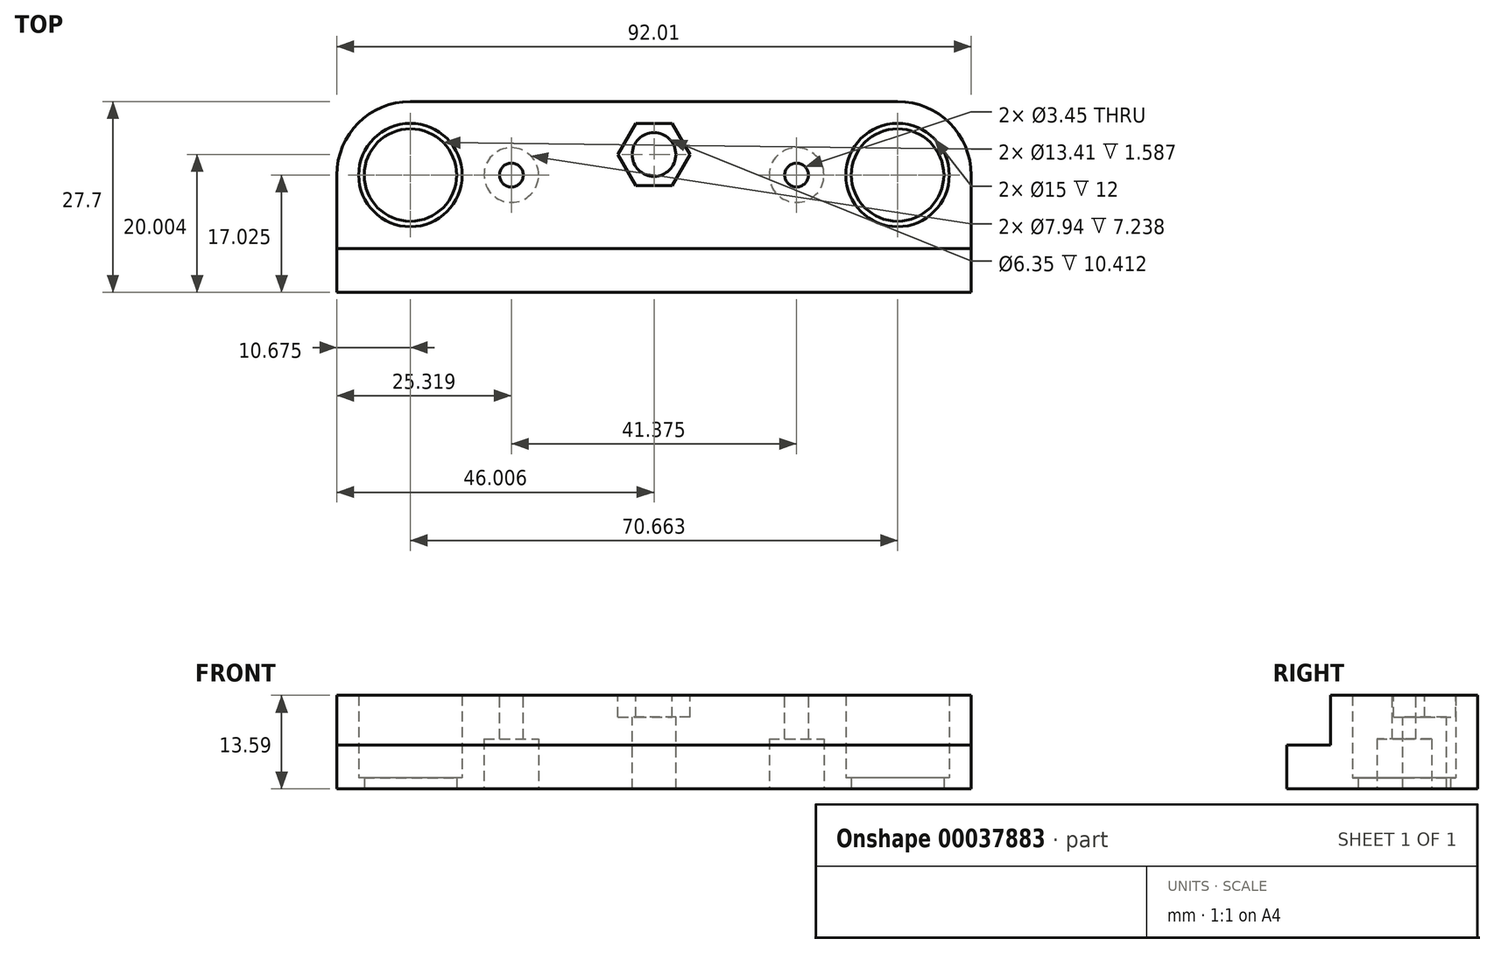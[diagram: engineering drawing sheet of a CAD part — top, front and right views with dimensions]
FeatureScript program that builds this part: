
annotation { "Feature Type Name" : "Feature", "Feature Type Description" : "" }
export const myFeature = defineFeature(function(context is Context, id is Id, definition is map)
    precondition{}
    {
        {
            var Q0;
            Q0=qCreatedBy(makeId("Top.planeOp"),FACE);
            var sketch = newSketch(context, id + "F0", { "sketchPlane" : qUnion([Q0])});
            skLineSegment(sketch, "E0.bottom", {"start": v(0, 0) * mm, "end": v(92.01, 0) * mm});
            skLineSegment(sketch, "E0.top", {"start": v(0, -27.7) * mm, "end": v(92.01, -27.7) * mm});
            skLineSegment(sketch, "E0.left", {"start": v(0, 0) * mm, "end": v(0, -27.7) * mm});
            skLineSegment(sketch, "E0.right", {"start": v(92.01, 0) * mm, "end": v(92.01, -27.7) * mm});
            skLineSegment(sketch, "E1", {"start": v(10.67, 0) * mm, "end": v(10.67, -10.67) * mm, "construction": true});
            skLineSegment(sketch, "E2", {"start": v(10.67, -10.67) * mm, "end": v(0, -10.67) * mm, "construction": true});
            skLineSegment(sketch, "E3", {"start": v(92.01, -10.67) * mm, "end": v(81.34, -10.67) * mm, "construction": true});
            skCircle(sketch, "E4", {"center": v(10.67, -10.67) * mm, "radius": 6.7 * mm});
            skCircle(sketch, "E5", {"center": v(81.34, -10.67) * mm, "radius": 6.7 * mm});
            skSolve(sketch);
        }
        {
            var Q0;
            Q0 = qSketchRegion(id + "F0", true);
            extrude(context, id + "F1", {"entities" : qUnion([Q0]), "depth" : 1.59 * mm});
        }
        {
            var Q0;
            Q0=makeQuery(id+"F1.opExtrude","SWEPT_EDGE",EDGE,{"disambiguationData":[OSD([sQuery(id+"F0.wireOp",EDGE,"E0.bottom"),sQuery(id+"F0.wireOp",EDGE,"E0.left")])]});
            var Q1;
            Q1=makeQuery(id+"F1.opExtrude","SWEPT_EDGE",EDGE,{"disambiguationData":[OSD([sQuery(id+"F0.wireOp",EDGE,"E0.bottom"),sQuery(id+"F0.wireOp",EDGE,"E0.right")])]});
            fillet(context, id + "F2", {"entities" : qUnion([Q0, Q1]), "radius" : 10.67 * mm, "tangentPropagation" : true, "allowEdgeOverflow" : false});
        }
        {
            var Q0;
            Q0=makeQuery(id+"F1.opExtrude","CAP_FACE",FACE,{"disambiguationData":[OSD([sQuery(id+"F0.wireOp",EDGE,"E0.bottom"),sQuery(id+"F0.wireOp",EDGE,"E0.top"),sQuery(id+"F0.wireOp",EDGE,"E0.left"),sQuery(id+"F0.wireOp",EDGE,"E0.right"),sQuery(id+"F0.wireOp",EDGE,"E4"),sQuery(id+"F0.wireOp",EDGE,"E5")])],"isStart":false});
            var sketch = newSketch(context, id + "F3", { "sketchPlane" : qUnion([Q0])});
            skLineSegment(sketch, "E6.bottom", {"start": v(0, -10.67) * mm, "end": v(92.01, -10.67) * mm, "construction": true});
            skLineSegment(sketch, "E6.top", {"start": v(0, -21.35) * mm, "end": v(92.01, -21.35) * mm});
            skLineSegment(sketch, "E6.left", {"start": v(0, -10.67) * mm, "end": v(0, -21.35) * mm});
            skLineSegment(sketch, "E6.right", {"start": v(92.01, -10.67) * mm, "end": v(92.01, -21.35) * mm});
            skLineSegment(sketch, "E7", {"start": v(46, -21.35) * mm, "end": v(46, -27.7) * mm, "construction": true});
            skPoint(sketch, "E7.endSnap0", {"position": v(46, -27.7) * mm});
            skCircle(sketch, "E8", {"center": v(10.67, -10.67) * mm, "radius": 7.5 * mm});
            skCircle(sketch, "E9", {"center": v(81.34, -10.67) * mm, "radius": 7.5 * mm});
            skSolve(sketch);
        }
        {
            var Q0;
            Q0=makeQuery(id+"F3.imprint","IMPRINT",FACE,{"disambiguationData":[TD([[makeQuery(id+"F3.imprint","IMPRINT",EDGE,{"derivedFrom":sQuery(id+"F3.wireOp",EDGE,"E6.top")}),1.0]])]});
            extrude(context, id + "F4", {"entities" : qUnion([Q0]), "operationType" : NewBodyOperationType.ADD, "depth" : 12 * mm});
        }
        {
            var Q0;
            {var subQ0=sQuery(id+"F0.wireOp",EDGE,"E0.top");var subQ1=sQuery(id+"F0.wireOp",EDGE,"E0.left");var subQ2=sQuery(id+"F0.wireOp",EDGE,"E0.right");Q0=makeQuery(id+"F4.boolean.opBoolean","SPLIT",FACE,{"disambiguationData":[TD([makeQuery(id+"F1.opExtrude","SWEPT_FACE",FACE,{"disambiguationData":[OSD([subQ0])]})])],"derivedFrom":makeQuery(id+"F1.opExtrude","CAP_FACE",FACE,{"disambiguationData":[OSD([sQuery(id+"F0.wireOp",EDGE,"E0.bottom"),subQ0,subQ1,subQ2,sQuery(id+"F0.wireOp",EDGE,"E4"),sQuery(id+"F0.wireOp",EDGE,"E5")])],"isStart":false})});}
            extrude(context, id + "F5", {"entities" : qUnion([Q0]), "operationType" : NewBodyOperationType.ADD, "depth" : 4.76 * mm});
        }
        {
            var Q0;
            Q0=makeQuery(id+"F4.opExtrude","CAP_FACE",FACE,{"disambiguationData":[OSD([sQuery(id+"F0.wireOp",EDGE,"E0.bottom"),sQuery(id+"F0.wireOp",EDGE,"E0.top"),sQuery(id+"F0.wireOp",EDGE,"E0.left"),sQuery(id+"F0.wireOp",EDGE,"E0.right"),sQuery(id+"F0.wireOp",EDGE,"E4"),sQuery(id+"F0.wireOp",EDGE,"E5"),sQuery(id+"F3.wireOp",EDGE,"E6.top"),sQuery(id+"F3.wireOp",EDGE,"E6.left"),sQuery(id+"F3.wireOp",EDGE,"E6.right"),sQuery(id+"F3.wireOp",EDGE,"E8"),sQuery(id+"F3.wireOp",EDGE,"E9")])],"isStart":false});
            var sketch = newSketch(context, id + "F6", { "sketchPlane" : qUnion([Q0])});
            skLineSegment(sketch, "E10", {"start": v(25.32, -10.67) * mm, "end": v(66.7, -10.67) * mm, "construction": true});
            skCircle(sketch, "E11", {"center": v(25.32, -10.67) * mm, "radius": 7.14 * mm, "construction": true});
            skPoint(sketch, "E12", {"position": v(46, -10.67) * mm});
            skCircle(sketch, "E13", {"center": v(25.32, -10.67) * mm, "radius": 1.73 * mm});
            skCircle(sketch, "E14", {"center": v(66.7, -10.67) * mm, "radius": 1.73 * mm});
            skLineSegment(sketch, "E15", {"start": v(46, -10.67) * mm, "end": v(46, -21.35) * mm, "construction": true});
            skLineSegment(sketch, "E16", {"start": v(46, -10.67) * mm, "end": v(46, -7.7) * mm, "construction": true});
            skCircle(sketch, "E17", {"center": v(46, -7.7) * mm, "radius": 3.18 * mm});
            skSolve(sketch);
        }
        {
            var Q0;
            Q0 = qSketchRegion(id + "F6", true);
            var Q1;
            Q1=makeQuery(id+"F1.opExtrude","CAP_FACE",FACE,{"disambiguationData":[OSD([sQuery(id+"F0.wireOp",EDGE,"E0.bottom"),sQuery(id+"F0.wireOp",EDGE,"E0.top"),sQuery(id+"F0.wireOp",EDGE,"E0.left"),sQuery(id+"F0.wireOp",EDGE,"E0.right"),sQuery(id+"F0.wireOp",EDGE,"E4"),sQuery(id+"F0.wireOp",EDGE,"E5")])],"isStart":true});
            extrude(context, id + "F7", {"entities" : qUnion([Q0]), "operationType" : NewBodyOperationType.REMOVE, "endBound" : BoundingType.UP_TO_SURFACE, "oppositeDirection" : true, "endBoundEntityFace" : qUnion([Q1]), "depth" : 25.4 * mm});
        }
        {
            var Q0;
            Q0=makeQuery(id+"F1.opExtrude","CAP_FACE",FACE,{"disambiguationData":[OSD([sQuery(id+"F0.wireOp",EDGE,"E0.bottom"),sQuery(id+"F0.wireOp",EDGE,"E0.top"),sQuery(id+"F0.wireOp",EDGE,"E0.left"),sQuery(id+"F0.wireOp",EDGE,"E0.right"),sQuery(id+"F0.wireOp",EDGE,"E4"),sQuery(id+"F0.wireOp",EDGE,"E5")])],"isStart":true});
            var sketch = newSketch(context, id + "F8", { "sketchPlane" : qUnion([Q0])});
            skCircle(sketch, "E18", {"center": v(66.7, 10.67) * mm, "radius": 3.97 * mm});
            skCircle(sketch, "E19", {"center": v(25.32, 10.67) * mm, "radius": 3.97 * mm});
            skSolve(sketch);
        }
        {
            var Q0;
            Q0 = qSketchRegion(id + "F8", true);
            extrude(context, id + "F9", {"entities" : qUnion([Q0]), "operationType" : NewBodyOperationType.REMOVE, "oppositeDirection" : true, "depth" : 7.24 * mm});
        }
        {
            var Q0;
            Q0=makeQuery(id+"F4.opExtrude","CAP_FACE",FACE,{"disambiguationData":[OSD([sQuery(id+"F0.wireOp",EDGE,"E0.bottom"),sQuery(id+"F0.wireOp",EDGE,"E0.top"),sQuery(id+"F0.wireOp",EDGE,"E0.left"),sQuery(id+"F0.wireOp",EDGE,"E0.right"),sQuery(id+"F0.wireOp",EDGE,"E4"),sQuery(id+"F0.wireOp",EDGE,"E5"),sQuery(id+"F3.wireOp",EDGE,"E6.top"),sQuery(id+"F3.wireOp",EDGE,"E6.left"),sQuery(id+"F3.wireOp",EDGE,"E6.right"),sQuery(id+"F3.wireOp",EDGE,"E8"),sQuery(id+"F3.wireOp",EDGE,"E9")])],"isStart":false});
            var sketch = newSketch(context, id + "F10", { "sketchPlane" : qUnion([Q0])});
            skCircle(sketch, "E20.cCircle", {"center": v(46, -7.7) * mm, "radius": 4.52 * mm, "construction": true});
            skLineSegment(sketch, "E20.0", {"start": v(43.4, -3.17) * mm, "end": v(48.62, -3.17) * mm});
            skLineSegment(sketch, "E20.1", {"start": v(48.62, -3.17) * mm, "end": v(51.23, -7.7) * mm});
            skLineSegment(sketch, "E20.2", {"start": v(51.23, -7.7) * mm, "end": v(48.62, -12.22) * mm});
            skLineSegment(sketch, "E20.3", {"start": v(48.62, -12.22) * mm, "end": v(43.4, -12.22) * mm});
            skLineSegment(sketch, "E20.4", {"start": v(43.4, -12.22) * mm, "end": v(40.79, -7.7) * mm});
            skLineSegment(sketch, "E20.5", {"start": v(40.79, -7.7) * mm, "end": v(43.4, -3.17) * mm});
            skPoint(sketch, "E20.0.midPoint", {"position": v(46, -3.17) * mm});
            skSolve(sketch);
        }
        {
            var Q0;
            Q0 = qSketchRegion(id + "F10", true);
            extrude(context, id + "F11", {"entities" : qUnion([Q0]), "operationType" : NewBodyOperationType.REMOVE, "oppositeDirection" : true, "depth" : 3.17 * mm});
        }
    });
